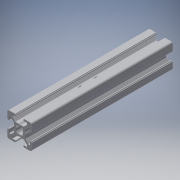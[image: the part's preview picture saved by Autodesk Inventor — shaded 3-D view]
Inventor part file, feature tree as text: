
AUTODESK INVENTOR PART (.ipt)
format: ipt  version: 2016 (Build 200138000, 138)  size: 405,504 bytes
history: native  units: in
note: dims shown in document units (in); Inventor stores cm internally (conversion verified against a paired STEP export)
features: other x3, sketch x2, extrude x1, hole x1, mirror x1
ambient origin geometry x8: Origin, YZ Plane, XZ Plane, XY Plane, X Axis, Y Axis, Z Axis, Center Point
bodies: Solid1 (feature_tree)
feature tree (8):
  other  "Blocks"
  extrude  "Extrusion1"  Depth=2.0in
  hole  "Hole1"  [1 undecoded]
  mirror  "Mirror1"
  sketch  "Sketch1"  dims[d1=0.0in d5=2.0in]
  other  "20x20"
  sketch  "Sketch3"  dims[d6=0.187in d7=0.75in d8=0.375in d9=0.25in d10=0.5635in d11=1.0in d12=0.8108in d13=1.0in d14=1.0in]
  other  "20x20:1"
note: 1 required parameter value undecoded (feature->parameter linkage not recoverable at this tier; creation-order binding heuristic only, values carry confidence <= 0.55)
